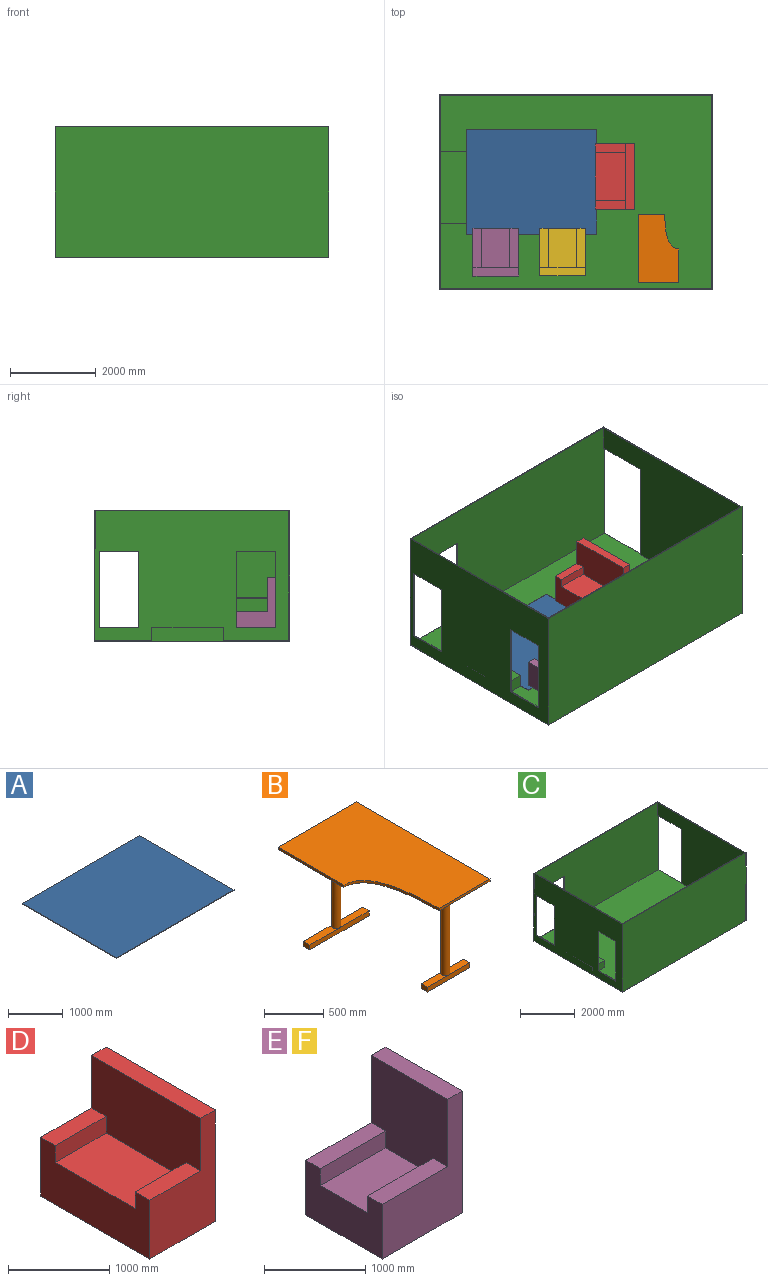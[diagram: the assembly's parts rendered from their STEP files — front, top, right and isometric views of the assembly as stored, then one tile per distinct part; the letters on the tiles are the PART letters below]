
ASSEMBLY  parts=6 mates=6
PART A: 6 faces, bbox 3048x2438.4x12.7 mm
  f0: plane 2438.4x12.7mm, normal (-1,0,0), area 30967.7mm2, adj f1,f3,f4,f5
  f1: plane 3048x12.7mm, normal (0,-1,0), area 38709.6mm2, adj f0,f2,f4,f5
  f2: plane 2438.4x12.7mm, normal (1,0,0), area 30967.7mm2, adj f1,f3,f4,f5
  f3: plane 3048x12.7mm, normal (0,1,0), area 38709.6mm2, adj f0,f2,f4,f5
  f4: plane 3048x2438.4mm, normal (0,0,1), area 7432243.2mm2, adj f0,f1,f2,f3
  f5: plane 3048x2438.4mm, normal (0,0,-1), area 7432243.2mm2, adj f0,f1,f2,f3
PART B: 23 faces, bbox 939.8x1600.2x990.6 mm
  f0: plane 609.6x25.4mm, normal (0,-1,0), area 15483.8mm2, adj f1,f4,f5,f6
  f1: plane 1600.2x25.4mm, normal (1,0,0), area 40645.1mm2, adj f0,f2,f5,f6
  f2: plane 939.8x25.4mm, normal (0,1,0), area 23870.9mm2, adj f1,f3,f5,f6
  f3: plane 787.4x25.4mm, normal (-1,0,0), area 20000mm2, adj f2,f4,f5,f6
  f4: extruded ~812.8x330.2mm, area 24405.4mm2, adj f0,f3,f5,f6
  f5: plane 1600.2x939.8mm, normal (0,0,1), area 1280212.5mm2, adj f0,f1,f2,f3,f4
  f6: plane 1600.2x939.8mm, normal (0,0,-1), area 1271091.8mm2, adj f0,f1,f2,f3,f4,f7,f8
  f7: cylinder r=38.1mm len=914.4mm, axis (0,0,1), area 218897.6mm2, adj f6,f9,f10
  f8: cylinder r=38.1mm len=914.4mm, axis (0,0,1), area 218897.6mm2, adj f6,f16,f17
  f9: plane 254x76.2mm, normal (0,0,1), area 17074.6mm2, adj f7,f11,f12,f14
  f10: plane 254x76.2mm, normal (0,0,1), area 17074.6mm2, adj f7,f12,f13,f14
  f11: plane 76.2x50.8mm, normal (1,0,0), area 3871mm2, adj f9,f12,f14,f15
  f12: plane 508x50.8mm, normal (0,-1,0), area 25806.4mm2, adj f9,f10,f11,f13,f15
  f13: plane 76.2x50.8mm, normal (-1,0,0), area 3871mm2, adj f10,f12,f14,f15
  f14: plane 508x50.8mm, normal (0,1,0), area 25806.4mm2, adj f9,f10,f11,f13,f15
  f15: plane 508x76.2mm, normal (0,0,-1), area 38709.6mm2, adj f11,f12,f13,f14
  f16: plane 355.6x76.2mm, normal (0,0,1), area 24816.5mm2, adj f8,f18,f19,f21
  f17: plane 355.6x76.2mm, normal (0,0,1), area 24816.5mm2, adj f8,f19,f20,f21
  f18: plane 76.2x50.8mm, normal (1,0,0), area 3871mm2, adj f16,f19,f21,f22
  f19: plane 711.2x50.8mm, normal (0,-1,0), area 36129mm2, adj f16,f17,f18,f20,f22
  f20: plane 76.2x50.8mm, normal (-1,0,0), area 3871mm2, adj f17,f19,f21,f22
  f21: plane 711.2x50.8mm, normal (0,1,0), area 36129mm2, adj f16,f17,f18,f20,f22
  f22: plane 711.2x76.2mm, normal (0,0,-1), area 54193.4mm2, adj f18,f19,f20,f21
PART C: 27 faces, bbox 6400.8x4572x3048 mm
  f0: plane 4572x3048mm, normal (-1,0,0), area 10683849.6mm2, adj f4,f6,f7,f8,f19,f20,f21,f22
  f1: plane 4546.6x3022.6mm, normal (1,0,0), area 9957399.4mm2, adj f2,f3,f4,f6,f10,f13,f15,f16
  f2: plane 6375.4x4546.6mm, normal (0,0,1), area 27757363.8mm2, adj f1,f3,f4,f5,f9,f10,f12,f14
  f3: plane 6375.4x3022.6mm, normal (0,-1,0), area 16003839mm2, adj f1,f2,f5,f6,f9,f11,f13,f14
  f4: plane 6400.8x3048mm, normal (0,1,0), area 16258032mm2, adj f0,f1,f2,f5,f6,f8,f13,f14
  f5: plane 4572x3048mm, normal (1,0,0), area 10962558.7mm2, adj f2,f3,f4,f6,f7,f8,f11,f12
  f6: plane 6400.8x4572mm, normal (0,0,1), area 554837.6mm2, adj f0,f1,f3,f4,f5,f7,f9,f10
  f7: plane 6400.8x3048mm, normal (0,-1,0), area 19509638.4mm2, adj f0,f5,f6,f8
  f8: plane 6400.8x4572mm, normal (0,0,-1), area 29264457.6mm2, adj f0,f4,f5,f7
  f9: plane 4521.2x3022.6mm, normal (-1,0,0), area 10692881.8mm2, adj f2,f3,f6,f10,f11,f12
  f10: plane 6350x3022.6mm, normal (0,1,0), area 19193510mm2, adj f1,f2,f6,f9
  f11: plane 1219.2x25.4mm, normal (0,0,-1), area 30967.7mm2, adj f3,f5,f9,f12
  f12: plane 2438.4x25.4mm, normal (0,1,0), area 61935.4mm2, adj f2,f5,f9,f11
  f13: plane 1524x25.4mm, normal (0,0,-1), area 38709.6mm2, adj f1,f3,f4,f14
  f14: plane 2133.6x25.4mm, normal (-1,0,0), area 54193.4mm2, adj f2,f3,f4,f13
  f15: plane 609.6x304.8mm, normal (0,1,0), area 185806.1mm2, adj f1,f2,f17,f18
  f16: plane 609.6x304.8mm, normal (0,-1,0), area 185806.1mm2, adj f1,f2,f17,f18
  f17: plane 1676.4x304.8mm, normal (1,0,0), area 510966.7mm2, adj f2,f15,f16,f18
  f18: plane 1676.4x609.6mm, normal (0,0,1), area 1021933.4mm2, adj f1,f15,f16,f17
  f19: plane 914.4x25.4mm, normal (0,0,1), area 23225.8mm2, adj f0,f1,f20,f22
  f20: plane 1778x25.4mm, normal (0,-1,0), area 45161.2mm2, adj f0,f1,f19,f21
  f21: plane 914.4x25.4mm, normal (0,0,-1), area 23225.8mm2, adj f0,f1,f20,f22
  f22: plane 1778x25.4mm, normal (0,1,0), area 45161.2mm2, adj f0,f1,f19,f21
  f23: plane 914.4x25.4mm, normal (0,0,1), area 23225.8mm2, adj f0,f1,f24,f26
  f24: plane 1778x25.4mm, normal (0,-1,0), area 45161.2mm2, adj f0,f1,f23,f25
  f25: plane 914.4x25.4mm, normal (0,0,-1), area 23225.8mm2, adj f0,f1,f24,f26
  f26: plane 1778x25.4mm, normal (0,1,0), area 45161.2mm2, adj f0,f1,f23,f25
PART D: 12 faces, bbox 914.4x1524x1346.2 mm
  f0: plane 711.2x203.2mm, normal (0,0,1), area 144515.8mm2, adj f2,f5,f7,f8
  f1: plane 1117.6x711.2mm, normal (0,0,1), area 794837.1mm2, adj f2,f7,f8,f9
  f2: plane 1524x711.2mm, normal (-1,0,0), area 856772.5mm2, adj f0,f1,f3,f5,f6,f7,f9,f10
  f3: plane 1346.2x914.4mm, normal (0,-1,0), area 779353.3mm2, adj f2,f4,f6,f8,f10,f11
  f4: plane 1524x1346.2mm, normal (1,0,0), area 2051608.8mm2, adj f3,f5,f6,f11
  f5: plane 1346.2x914.4mm, normal (0,1,0), area 779353.3mm2, adj f0,f2,f4,f6,f8,f11
  f6: plane 1524x914.4mm, normal (0,0,-1), area 1393545.6mm2, adj f2,f3,f4,f5
  f7: plane 711.2x203.2mm, normal (0,-1,0), area 144515.8mm2, adj f0,f1,f2,f8
  f8: plane 1524x838.2mm, normal (-1,0,0), area 1194836.3mm2, adj f0,f1,f3,f5,f7,f9,f10,f11
  f9: plane 711.2x203.2mm, normal (0,1,0), area 144515.8mm2, adj f1,f2,f8,f10
  f10: plane 711.2x203.2mm, normal (0,0,1), area 144515.8mm2, adj f2,f3,f8,f9
  f11: plane 1524x203.2mm, normal (0,0,1), area 309676.8mm2, adj f3,f4,f5,f8
PART E: 12 faces, bbox 1117.6x1066.8x1473.2 mm
  f0: plane 914.4x203.2mm, normal (0,0,1), area 185806.1mm2, adj f2,f5,f7,f8
  f1: plane 914.4x660.4mm, normal (0,0,1), area 603869.8mm2, adj f2,f7,f8,f9
  f2: plane 1066.8x660.4mm, normal (-1,0,0), area 570321.4mm2, adj f0,f1,f3,f5,f6,f7,f9,f10
  f3: plane 1473.2x1117.6mm, normal (0,-1,0), area 903224mm2, adj f2,f4,f6,f8,f10,f11
  f4: plane 1473.2x1066.8mm, normal (1,0,0), area 1571609.8mm2, adj f3,f5,f6,f11
  f5: plane 1473.2x1117.6mm, normal (0,1,0), area 903224mm2, adj f0,f2,f4,f6,f8,f11
  f6: plane 1117.6x1066.8mm, normal (0,0,-1), area 1192255.7mm2, adj f2,f3,f4,f5
  f7: plane 914.4x203.2mm, normal (0,-1,0), area 185806.1mm2, adj f0,f1,f2,f8
  f8: plane 1066.8x1016mm, normal (-1,0,0), area 1001288.3mm2, adj f0,f1,f3,f5,f7,f9,f10,f11
  f9: plane 914.4x203.2mm, normal (0,1,0), area 185806.1mm2, adj f1,f2,f8,f10
  f10: plane 914.4x203.2mm, normal (0,0,1), area 185806.1mm2, adj f2,f3,f8,f9
  f11: plane 1066.8x203.2mm, normal (0,0,1), area 216773.8mm2, adj f3,f4,f5,f8
PART F: same geometry as E
PLACE A t=(-5765.8,1305.98,25.4)mm
PLACE B rot(axis=(0,0,1),180deg) t=(-797.91,167.78,990.6)mm
PLACE C t=(-3200.4,2286,0)mm
PLACE D t=(-2753.98,1887.83,25.4)mm
PLACE E rot(axis=(0,0,-1),90deg) t=(-5608.74,1439.89,25.4)mm
PLACE F rot(axis=(0,0,-1),90deg) t=(-4047.57,1444.69,25.4)mm
MATE planar C.f2 <-> B.f7  axis (0,0,1) through (-3094.54,2287.27,25.4)mm
MATE planar A.f0 <-> C.f17  axis (-1,0,0) through (-5765.8,2525.18,31.75)mm
MATE planar C.f2 <-> F.f6  axis (0,0,1) through (-3094.54,2287.27,25.4)mm
MATE planar E.f6 <-> C.f2  axis (0,0,-1) through (-5075.34,881.09,25.4)mm
MATE planar C.f2 <-> D.f6  axis (0,0,1) through (-3094.54,2287.27,25.4)mm
MATE planar C.f2 <-> A.f5  axis (0,0,1) through (-3094.54,2287.27,25.4)mm
